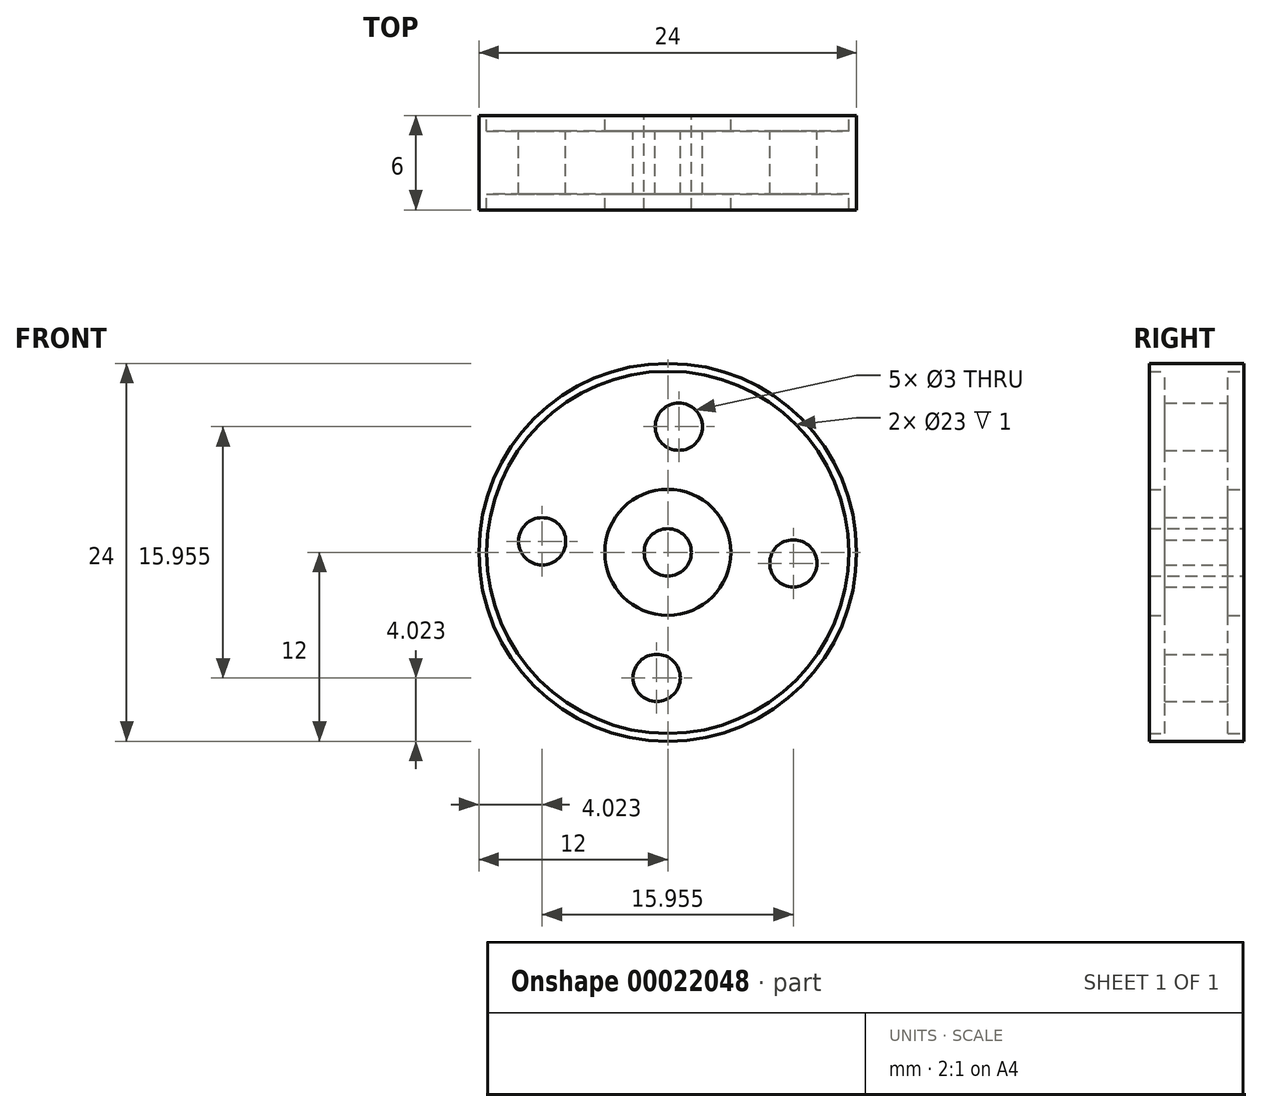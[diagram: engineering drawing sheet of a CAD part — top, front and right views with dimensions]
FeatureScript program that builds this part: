
annotation { "Feature Type Name" : "Feature", "Feature Type Description" : "" }
export const myFeature = defineFeature(function(context is Context, id is Id, definition is map)
    precondition{}
    {
        {
            var Q0;
            Q0=qCreatedBy(makeId("Front.planeOp"),FACE);
            var sketch = newSketch(context, id + "F0", { "sketchPlane" : qUnion([Q0])});
            skCircle(sketch, "E0", {"center": v(0, 0) * mm, "radius": 11.5 * mm});
            skCircle(sketch, "E1", {"center": v(0, 0) * mm, "radius": 4 * mm});
            skCircle(sketch, "E2", {"center": v(0, 0) * mm, "radius": 1.5 * mm});
            skCircle(sketch, "E3", {"center": v(-7.98, 0.7) * mm, "radius": 1.5 * mm});
            skLineSegment(sketch, "E4", {"start": v(-9.48, 0.73) * mm, "end": v(-11.48, 0.73) * mm});
            skLineSegment(sketch, "E5.trimOffspring", {"start": v(-1.5, 0.15) * mm, "end": v(1.49, -0.18) * mm});
            skCircle(sketch, "E6.1.0", {"center": v(-0.7, -7.98) * mm, "radius": 1.5 * mm});
            skCircle(sketch, "E6.2.0", {"center": v(7.98, -0.7) * mm, "radius": 1.5 * mm});
            skCircle(sketch, "E6.3.0", {"center": v(0.7, 7.98) * mm, "radius": 1.5 * mm});
            skCircle(sketch, "E7", {"center": v(0, 0) * mm, "radius": 12 * mm});
            skSolve(sketch);
        }
        {
            var Q0;
            Q0=makeQuery(id+"F0.imprint","IMPRINT",FACE,{"disambiguationData":[TD([[makeQuery(id+"F0.imprint","IMPRINT",EDGE,{"derivedFrom":sQuery(id+"F0.wireOp",EDGE,"E0")}),1.0]])]});
            extrude(context, id + "F1", {"entities" : qUnion([Q0]), "endBound" : BoundingType.SYMMETRIC, "depth" : 4 * mm});
        }
        {
            var Q0;
            Q0=makeQuery(id+"F0.imprint","IMPRINT",FACE,{"disambiguationData":[TD([[makeQuery(id+"F0.imprint","IMPRINT",EDGE,{"derivedFrom":sQuery(id+"F0.wireOp",EDGE,"E1")}),1.0]])]});
            extrude(context, id + "F2", {"entities" : qUnion([Q0]), "operationType" : NewBodyOperationType.ADD, "endBound" : BoundingType.SYMMETRIC, "depth" : 6 * mm});
        }
        {
            var Q0;
            Q0=makeQuery(id+"F0.imprint","IMPRINT",FACE,{"disambiguationData":[TD([[makeQuery(id+"F0.imprint","IMPRINT",EDGE,{"derivedFrom":sQuery(id+"F0.wireOp",EDGE,"E0")}),-1.0]])]});
            extrude(context, id + "F3", {"entities" : qUnion([Q0]), "operationType" : NewBodyOperationType.ADD, "endBound" : BoundingType.SYMMETRIC, "depth" : 6 * mm});
        }
    });
